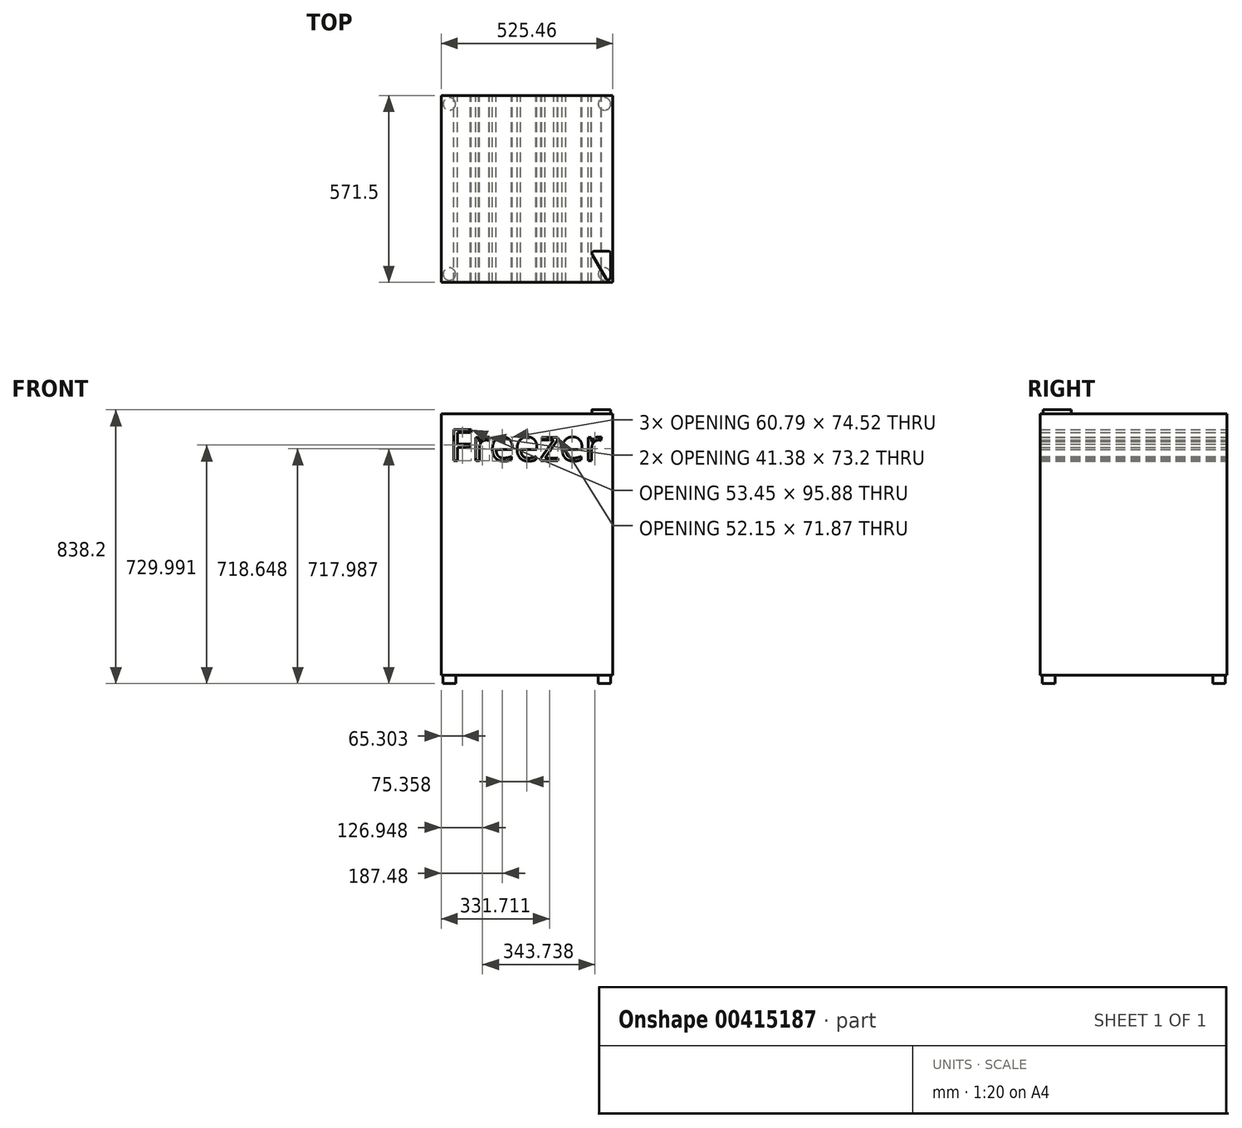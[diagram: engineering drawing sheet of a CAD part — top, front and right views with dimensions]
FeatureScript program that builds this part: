
annotation { "Feature Type Name" : "Feature", "Feature Type Description" : "" }
export const myFeature = defineFeature(function(context is Context, id is Id, definition is map)
    precondition{}
    {
        {
            var Q0;
            Q0=qCreatedBy(makeId("Front.planeOp"),FACE);
            var sketch = newSketch(context, id + "F0", { "sketchPlane" : qUnion([Q0])});
            skLineSegment(sketch, "E0.bottom", {"start": v(0, 874.39) * mm, "end": v(525.46, 874.39) * mm});
            skLineSegment(sketch, "E0.top", {"start": v(0, 74.29) * mm, "end": v(525.46, 74.29) * mm});
            skLineSegment(sketch, "E0.left", {"start": v(0, 874.39) * mm, "end": v(0, 74.29) * mm});
            skLineSegment(sketch, "E0.right", {"start": v(525.46, 874.39) * mm, "end": v(525.46, 74.29) * mm});
            skText(sketch, "E1", { "text": "Freezer", "fontName": "OpenSans-Regular.ttf"});
            const initialGuessF0  = {"E1": [0.0254, 0.73094, 1, 0, 0.0967]};
            skSetInitialGuess(sketch, initialGuessF0);
            skSolve(sketch);
        }
        {
            var Q0;
            Q0 = qSketchRegion(id + "F0", true);
            extrude(context, id + "F1", {"entities" : qUnion([Q0]), "depth" : 571.5 * mm, "offsetDistance" : 25.4 * mm});
        }
        {
            var Q0;
            Q0=makeQuery(id+"F1.opExtrude","SWEPT_FACE",FACE,{"disambiguationData":[OSD([sQuery(id+"F0.wireOp",EDGE,"E0.top")])]});
            var sketch = newSketch(context, id + "F2", { "sketchPlane" : qUnion([Q0])});
            skCircle(sketch, "E2", {"center": v(25.4, 25.4) * mm, "radius": 19.05 * mm});
            skLineSegment(sketch, "E3.bottom", {"start": v(25.4, 25.4) * mm, "end": v(500.06, 25.4) * mm, "construction": true});
            skLineSegment(sketch, "E3.top", {"start": v(25.4, 546.1) * mm, "end": v(500.06, 546.1) * mm, "construction": true});
            skLineSegment(sketch, "E3.left", {"start": v(25.4, 25.4) * mm, "end": v(25.4, 546.1) * mm, "construction": true});
            skLineSegment(sketch, "E3.right", {"start": v(500.06, 25.4) * mm, "end": v(500.06, 546.1) * mm, "construction": true});
            skCircle(sketch, "E4", {"center": v(25.4, 546.1) * mm, "radius": 19.05 * mm});
            skCircle(sketch, "E5", {"center": v(500.06, 546.1) * mm, "radius": 19.05 * mm});
            skCircle(sketch, "E6", {"center": v(500.06, 25.4) * mm, "radius": 19.05 * mm});
            skSolve(sketch);
        }
        {
            var Q0;
            Q0 = qSketchRegion(id + "F2", true);
            extrude(context, id + "F3", {"entities" : qUnion([Q0]), "operationType" : NewBodyOperationType.ADD, "depth" : 25.4 * mm, "offsetDistance" : 25.4 * mm});
        }
        {
            var Q0;
            Q0=makeQuery(id+"F1.opExtrude","SWEPT_FACE",FACE,{"disambiguationData":[OSD([sQuery(id+"F0.wireOp",EDGE,"E0.bottom")])]});
            var sketch = newSketch(context, id + "F4", { "sketchPlane" : qUnion([Q0])});
            skLineSegment(sketch, "E7", {"start": v(455.61, -476.25) * mm, "end": v(519.11, -476.25) * mm});
            skLineSegment(sketch, "E8", {"start": v(519.11, -476.25) * mm, "end": v(519.11, -584.2) * mm});
            skLineSegment(sketch, "E9", {"start": v(519.11, -584.2) * mm, "end": v(455.61, -476.25) * mm});
            skSolve(sketch);
        }
        {
            var Q0;
            Q0 = qSketchRegion(id + "F4", true);
            extrude(context, id + "F5", {"entities" : qUnion([Q0]), "operationType" : NewBodyOperationType.ADD, "depth" : 12.7 * mm, "offsetDistance" : 25.4 * mm});
        }
        {
            var Q0;
            Q0=makeQuery(id+"F5.opExtrude","SWEPT_EDGE",EDGE,{"disambiguationData":[OSD([sQuery(id+"F4.wireOp",EDGE,"E8"),sQuery(id+"F4.wireOp",EDGE,"E9")])]});
            var Q1;
            Q1=makeQuery(id+"F5.opExtrude","SWEPT_EDGE",EDGE,{"disambiguationData":[OSD([sQuery(id+"F4.wireOp",EDGE,"E7"),sQuery(id+"F4.wireOp",EDGE,"E8")])]});
            var Q2;
            Q2=makeQuery(id+"F5.opExtrude","SWEPT_EDGE",EDGE,{"disambiguationData":[OSD([sQuery(id+"F4.wireOp",EDGE,"E7"),sQuery(id+"F4.wireOp",EDGE,"E9")])]});
            fillet(context, id + "F6", {"entities" : qUnion([Q0, Q1, Q2]), "radius" : 7.62 * mm, "tangentPropagation" : true, "allowEdgeOverflow" : false});
        }
    });
